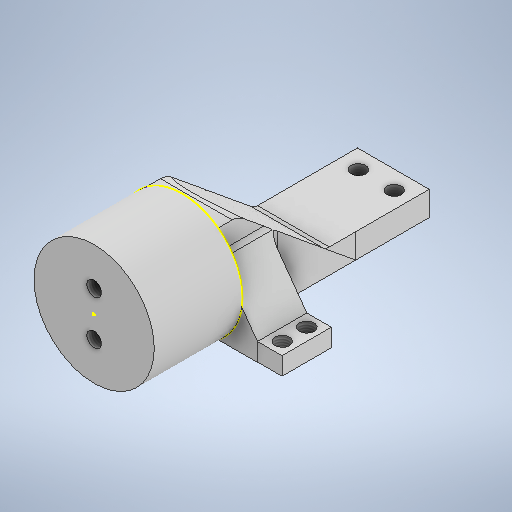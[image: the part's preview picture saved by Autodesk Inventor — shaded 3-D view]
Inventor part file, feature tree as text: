
AUTODESK INVENTOR PART (.ipt)
format: ipt  version: 2025.2 (Build 292293000, 293)  size: 453,120 bytes
history: native  units: in
note: dims shown in document units (in); Inventor stores cm internally (conversion verified against a paired STEP export)
features: sketch x16, extrude x14, thread x8, fillet x2, mirror x1
ambient origin geometry x8: Origin, YZ Plane, XZ Plane, XY Plane, X Axis, Y Axis, Z Axis, Center Point
bodies: Solid1 (feature_tree)
feature tree (41):
  sketch  "Sketch1"  dims[d0=0.9646in d1=0.1772in d2=0.1772in d3=0.1181in]
  extrude  "Extrusion1"  Depth=0.1772in
  thread  "Thread1"  [1 undecoded]
  thread  "Thread2"  [1 undecoded]
  sketch  "Sketch3"  dims[d7=0.7087in d8=0.0in d9=0.7087in d10=0.0in]
  extrude  "Extrusion2"  Depth=0.7087in TaperAngle=0.0deg
  extrude  "Extrusion3"  Depth=0.7087in TaperAngle=0.0deg
  extrude  "Extrusion4"  Depth=1.1024in TaperAngle=0.0deg
  extrude  "Extrusion5"  Depth=0.1969in TaperAngle=0.0deg
  extrude  "Extrusion6"  Depth=0.315in TaperAngle=0.0deg
  extrude  "Extrusion7"  Depth=0.3937in TaperAngle=0.0deg
  extrude  "Extrusion8"  Depth=0.1181in
  sketch  "Sketch11"  dims[d38=0.1969in d39=0.0in d40=0.1429in d41=0.0in]
  extrude  "Extrusion9"  Depth=0.3937in TaperAngle=0.0deg
  extrude  "Extrusion10"  Depth=0.1181in
  mirror  "Mirror2"
  extrude  "Extrusion11"  Depth=0.1429in TaperAngle=0.0deg
  extrude  "Extrusion12"  Depth=0.0787in TaperAngle=0.0deg
  thread  "Thread3"  [1 undecoded]
  thread  "Thread4"  [1 undecoded]
  thread  "Thread5"  [1 undecoded]
  thread  "Thread6"  [1 undecoded]
  thread  "Thread7"  [1 undecoded]
  thread  "Thread8"  [1 undecoded]
  sketch  "Sketch15"
  extrude  "Extrusion13"  [1 undecoded]
  extrude  "Extrusion14"  [1 undecoded]
  fillet  "Fillet1"  [1 undecoded]
  fillet  "Fillet2"  [1 undecoded]
  sketch  "Sketch2"  dims[d4=0.1181in d5=0.7087in d6=0.0in]
  sketch  "Sketch4"  dims[d11=1.1024in d12=0.0in d13=1.1024in d14=0.0in]
  sketch  "Sketch5"  dims[d16=0.1181in d18=0.1969in d19=0.0in]
  sketch  "Sketch6"  dims[d20=0.5752in d21=0.0in d22=0.315in d23=0.0in]
  sketch  "Sketch7"  dims[d24=0.3937in d25=0.0in d26=0.3937in d27=0.0in]
  sketch  "Sketch8"  dims[d28=0.1181in d29=0.1181in]
  sketch  "Sketch9"  dims[d30=0.3937in d31=0.0in d32=0.3937in d33=0.0in]
  sketch  "Sketch10"  dims[d34=0.1969in d35=0.0in d37=0.1181in]
  sketch  "Sketch13"  dims[d42=0.1429in d43=0.0in d44=0.1969in d45=0.0in d46=0.1969in d47=0.0in d48=0.1587in d49=0.0in d50=0.1602in d51=0.0in d52=0.0028in d53=0.0in d54=0.0028in d55=0.0in d56=0.0787in]
  sketch  "Sketch14"  dims[d57=0.0787in]
  sketch  "Sketch16"
  sketch  "Sketch17"
note: 12 required parameter values undecoded (feature->parameter linkage not recoverable at this tier; creation-order binding heuristic only, values carry confidence <= 0.55)
